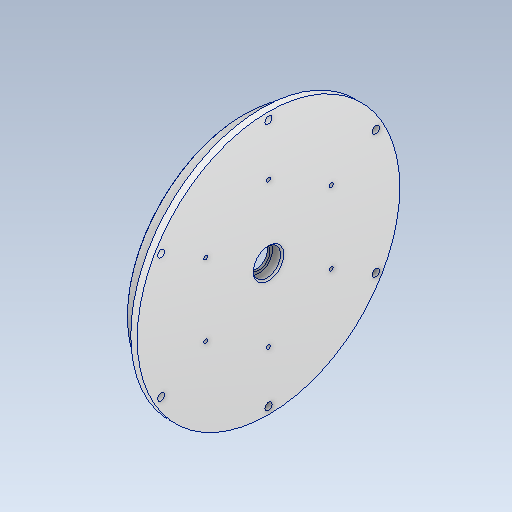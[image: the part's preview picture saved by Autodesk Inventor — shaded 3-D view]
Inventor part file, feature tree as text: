
AUTODESK INVENTOR PART (.ipt)
format: ipt  version: 2021 (Build 250183000, 183)  size: 209,408 bytes
history: native  units: mm
features: sketch x3, chamfer x2, hole x2, revolve x1, pattern_circular x1, projected_geometry x1
ambient origin geometry x8: Origin, YZ Plane, XZ Plane, XY Plane, X Axis, Y Axis, Z Axis, Center Point
bodies: Solid1 (feature_tree)
feature tree (10):
  revolve  "Revolution1"  [1 undecoded]
  chamfer  "Chamfer1"  Distance=6.0mm
  hole  "Hole1"  [1 undecoded]
  pattern_circular  "Circular Pattern1"  Angle=45.0deg  [1 undecoded]
  chamfer  "Chamfer2"  Distance=7.0mm
  hole  "Hole2"  [1 undecoded]
  sketch  "Sketch1"  dims[d6=69.57767mm d7=8.5mm]
  sketch  "Sketch2"  dims[d11=90.0deg]
  projected_geometry  "Projected Loop1"
  sketch  "Sketch3"  dims[d15=1.5mm d17=6.0mm d18=1.625mm d19=1.0mm d20=2.0mm d21=45.0deg d22=7.0mm d23=1.0mm d24=2.0mm d25=64.0mm d26=4.0mm d27=15.0mm d29=4.0mm d30=9.0mm d31=4.5mm d32=4.5mm d33=4.5mm d34=6.0mm d35=9.4mm d36=2.0mm d37=90.0deg d38=8.0mm d39=20.594885mm d40=60.0mm d41=360.0deg d43=0.4mm d44=2.0mm d45=45.0deg d46=90.0mm d47=60.0mm d49=360.0deg d51=2.459mm d52=5.0mm d53=9.4mm d54=2.0mm d55=90.0deg d56=6.5mm d57=20.594885mm]
note: 4 required parameter values undecoded (feature->parameter linkage not recoverable at this tier; creation-order binding heuristic only, values carry confidence <= 0.55)